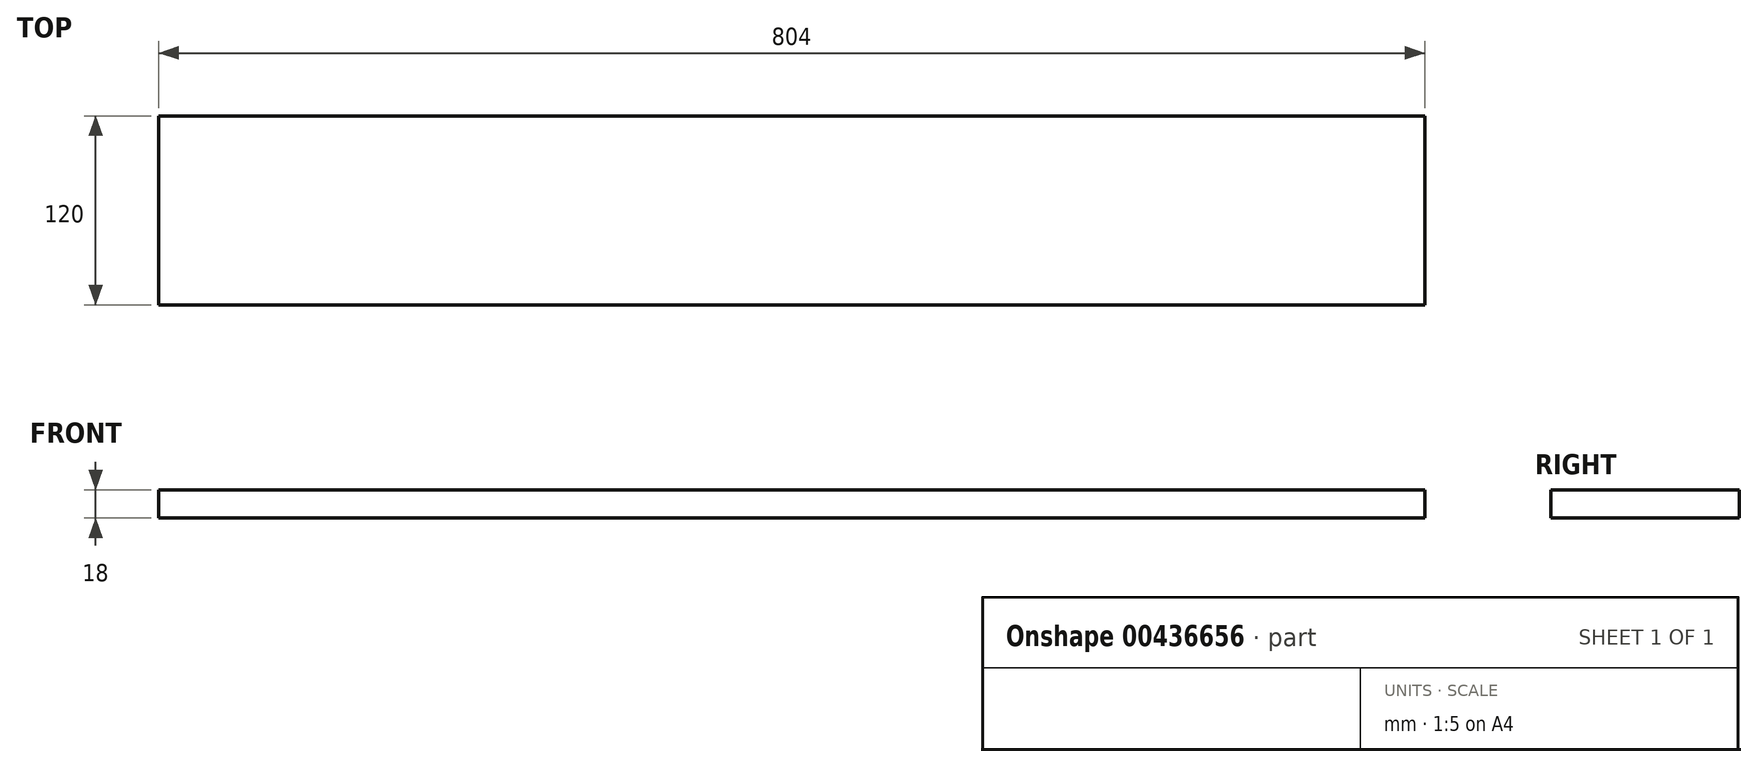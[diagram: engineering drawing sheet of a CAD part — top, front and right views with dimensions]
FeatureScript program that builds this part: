
annotation { "Feature Type Name" : "Feature", "Feature Type Description" : "" }
export const myFeature = defineFeature(function(context is Context, id is Id, definition is map)
    precondition{}
    {
        {
            var Q0;
            Q0=qCreatedBy(makeId("Right.planeOp"),FACE);
            var sketch = newSketch(context, id + "F0", { "sketchPlane" : qUnion([Q0])});
            skLineSegment(sketch, "E0.bottom", {"start": v(60, 9) * mm, "end": v(-60, 9) * mm});
            skLineSegment(sketch, "E0.top", {"start": v(60, -9) * mm, "end": v(-60, -9) * mm});
            skLineSegment(sketch, "E0.left", {"start": v(60, 9) * mm, "end": v(60, -9) * mm});
            skLineSegment(sketch, "E0.right", {"start": v(-60, 9) * mm, "end": v(-60, -9) * mm});
            skPoint(sketch, "E0.middle", {"position": v(0, 0) * mm});
            skSolve(sketch);
        }
        {
            var Q0;
            Q0 = qSketchRegion(id + "F0", true);
            extrude(context, id + "F1", {"entities" : qUnion([Q0]), "depth" : 804 * mm});
        }
    });
